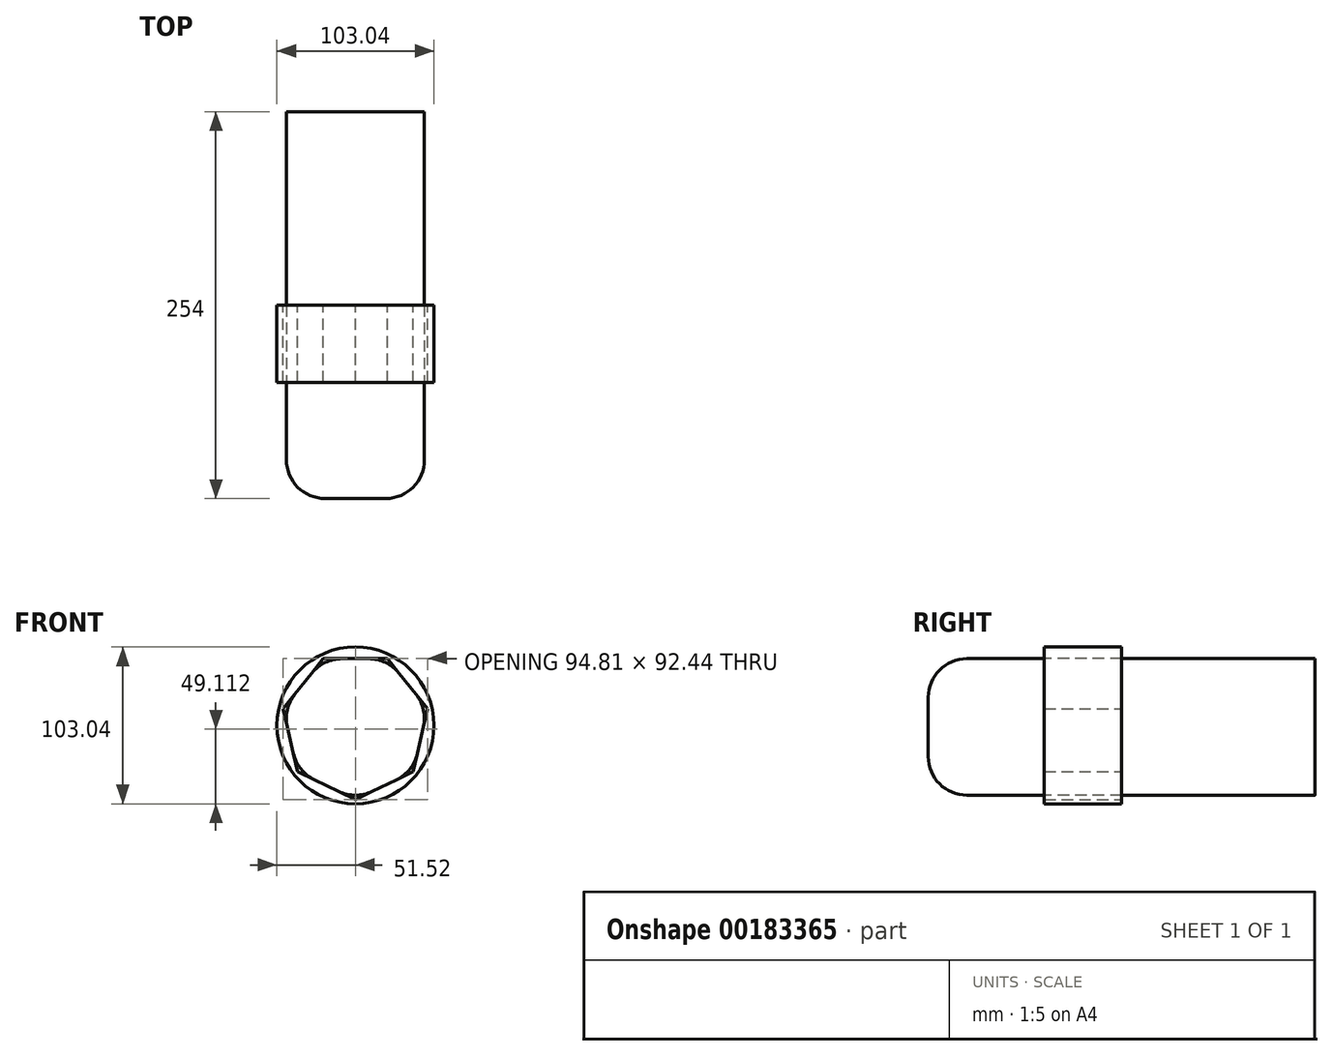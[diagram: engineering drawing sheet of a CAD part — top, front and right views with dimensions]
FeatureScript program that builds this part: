
annotation { "Feature Type Name" : "Feature", "Feature Type Description" : "" }
export const myFeature = defineFeature(function(context is Context, id is Id, definition is map)
    precondition{}
    {
        {
            var Q0;
            Q0=qCreatedBy(makeId("Front.planeOp"),FACE);
            var sketch = newSketch(context, id + "F0", { "sketchPlane" : qUnion([Q0])});
            skCircle(sketch, "E0.cCircle", {"center": v(0, 0) * mm, "radius": 43.81 * mm, "construction": true});
            skLineSegment(sketch, "E0.0", {"start": v(-21.1, 43.81) * mm, "end": v(21.1, 43.81) * mm});
            skLineSegment(sketch, "E0.1", {"start": v(21.1, 43.81) * mm, "end": v(47.4, 10.82) * mm});
            skLineSegment(sketch, "E0.2", {"start": v(47.4, 10.82) * mm, "end": v(38.02, -30.32) * mm});
            skLineSegment(sketch, "E0.3", {"start": v(38.02, -30.32) * mm, "end": v(0, -48.63) * mm});
            skLineSegment(sketch, "E0.4", {"start": v(0, -48.63) * mm, "end": v(-38.02, -30.32) * mm});
            skLineSegment(sketch, "E0.5", {"start": v(-38.02, -30.32) * mm, "end": v(-47.4, 10.82) * mm});
            skLineSegment(sketch, "E0.6", {"start": v(-47.4, 10.82) * mm, "end": v(-21.1, 43.81) * mm});
            skPoint(sketch, "E0.0.midPoint", {"position": v(0, 43.81) * mm});
            skCircle(sketch, "E1.0", {"center": v(0, 0) * mm, "radius": 51.52 * mm});
            skSolve(sketch);
        }
        {
            var Q0;
            Q0=makeQuery(id+"F0.imprint","IMPRINT",FACE,{"disambiguationData":[TD([[makeQuery(id+"F0.imprint","IMPRINT",EDGE,{"derivedFrom":sQuery(id+"F0.wireOp",EDGE,"E0.0")}),1.0]])]});
            extrude(context, id + "F1", {"entities" : qUnion([Q0]), "endBound" : BoundingType.SYMMETRIC, "depth" : 50.8 * mm});
        }
        {
            var Q0;
            Q0=makeQuery(id+"F1.opExtrude","CAP_FACE",FACE,{"disambiguationData":[OSD([sQuery(id+"F0.wireOp",EDGE,"E0.0"),sQuery(id+"F0.wireOp",EDGE,"E0.1"),sQuery(id+"F0.wireOp",EDGE,"E0.2"),sQuery(id+"F0.wireOp",EDGE,"E0.3"),sQuery(id+"F0.wireOp",EDGE,"E0.4"),sQuery(id+"F0.wireOp",EDGE,"E0.5"),sQuery(id+"F0.wireOp",EDGE,"E0.6"),sQuery(id+"F0.wireOp",EDGE,"E1.0")])],"isStart":true});
            var sketch = newSketch(context, id + "F2", { "sketchPlane" : qUnion([Q0])});
            skCircle(sketch, "E2.cCircle", {"center": v(0, 0) * mm, "radius": 43.81 * mm, "construction": true});
            skLineSegment(sketch, "E2.0", {"start": v(-21.1, 43.81) * mm, "end": v(21.1, 43.81) * mm});
            skLineSegment(sketch, "E2.1", {"start": v(21.1, 43.81) * mm, "end": v(47.4, 10.82) * mm});
            skLineSegment(sketch, "E2.2", {"start": v(47.4, 10.82) * mm, "end": v(38.02, -30.32) * mm});
            skLineSegment(sketch, "E2.3", {"start": v(38.02, -30.32) * mm, "end": v(0, -48.63) * mm});
            skLineSegment(sketch, "E2.4", {"start": v(0, -48.63) * mm, "end": v(-38.02, -30.32) * mm});
            skLineSegment(sketch, "E2.5", {"start": v(-38.02, -30.32) * mm, "end": v(-47.4, 10.82) * mm});
            skLineSegment(sketch, "E2.6", {"start": v(-47.4, 10.82) * mm, "end": v(-21.1, 43.81) * mm});
            skPoint(sketch, "E2.0.midPoint", {"position": v(0, 43.81) * mm});
            skSolve(sketch);
        }
        {
            var Q0;
            Q0=makeQuery(id+"F2.imprint","IMPRINT",FACE,{"disambiguationData":[TD([[makeQuery(id+"F2.imprint","IMPRINT",EDGE,{"derivedFrom":sQuery(id+"F2.wireOp",EDGE,"E2.0")}),1.0]])]});
            extrude(context, id + "F3", {"entities" : qUnion([Q0]), "endBound" : BoundingType.SYMMETRIC, "depth" : 254 * mm});
        }
        {
            var Q0;
            Q0=makeQuery(id+"F3.opExtrude","CAP_EDGE",EDGE,{"disambiguationData":[OSD([sQuery(id+"F2.wireOp",EDGE,"E2.0")])],"isStart":true});
            var Q1;
            Q1=makeQuery(id+"F3.opExtrude","CAP_FACE",FACE,{"disambiguationData":[OSD([sQuery(id+"F2.wireOp",EDGE,"E2.0"),sQuery(id+"F2.wireOp",EDGE,"E2.1"),sQuery(id+"F2.wireOp",EDGE,"E2.2"),sQuery(id+"F2.wireOp",EDGE,"E2.3"),sQuery(id+"F2.wireOp",EDGE,"E2.4"),sQuery(id+"F2.wireOp",EDGE,"E2.5"),sQuery(id+"F2.wireOp",EDGE,"E2.6")])],"isStart":true});
            var Q2;
            Q2=makeQuery(id+"F3.opExtrude","SWEPT_EDGE",EDGE,{"disambiguationData":[OSD([sQuery(id+"F2.wireOp",EDGE,"E2.5"),sQuery(id+"F2.wireOp",EDGE,"E2.6")])]});
            var Q3;
            Q3=makeQuery(id+"F3.opExtrude","SWEPT_EDGE",EDGE,{"disambiguationData":[OSD([sQuery(id+"F2.wireOp",EDGE,"E2.0"),sQuery(id+"F2.wireOp",EDGE,"E2.6")])]});
            var Q4;
            Q4=makeQuery(id+"F3.opExtrude","SWEPT_EDGE",EDGE,{"disambiguationData":[OSD([sQuery(id+"F2.wireOp",EDGE,"E2.0"),sQuery(id+"F2.wireOp",EDGE,"E2.1")])]});
            var Q5;
            Q5=makeQuery(id+"F3.opExtrude","SWEPT_EDGE",EDGE,{"disambiguationData":[OSD([sQuery(id+"F2.wireOp",EDGE,"E2.1"),sQuery(id+"F2.wireOp",EDGE,"E2.2")])]});
            var Q6;
            Q6=makeQuery(id+"F3.opExtrude","SWEPT_EDGE",EDGE,{"disambiguationData":[OSD([sQuery(id+"F2.wireOp",EDGE,"E2.2"),sQuery(id+"F2.wireOp",EDGE,"E2.3")])]});
            var Q7;
            Q7=makeQuery(id+"F3.opExtrude","SWEPT_EDGE",EDGE,{"disambiguationData":[OSD([sQuery(id+"F2.wireOp",EDGE,"E2.4"),sQuery(id+"F2.wireOp",EDGE,"E2.5")])]});
            var Q8;
            Q8=makeQuery(id+"F3.opExtrude","SWEPT_EDGE",EDGE,{"disambiguationData":[OSD([sQuery(id+"F2.wireOp",EDGE,"E2.3"),sQuery(id+"F2.wireOp",EDGE,"E2.4")])]});
            fillet(context, id + "F4", {"entities" : qUnion([Q0, Q1, Q2, Q3, Q4, Q5, Q6, Q7, Q8]), "radius" : 25.4 * mm, "tangentPropagation" : true, "allowEdgeOverflow" : false});
        }
    });
